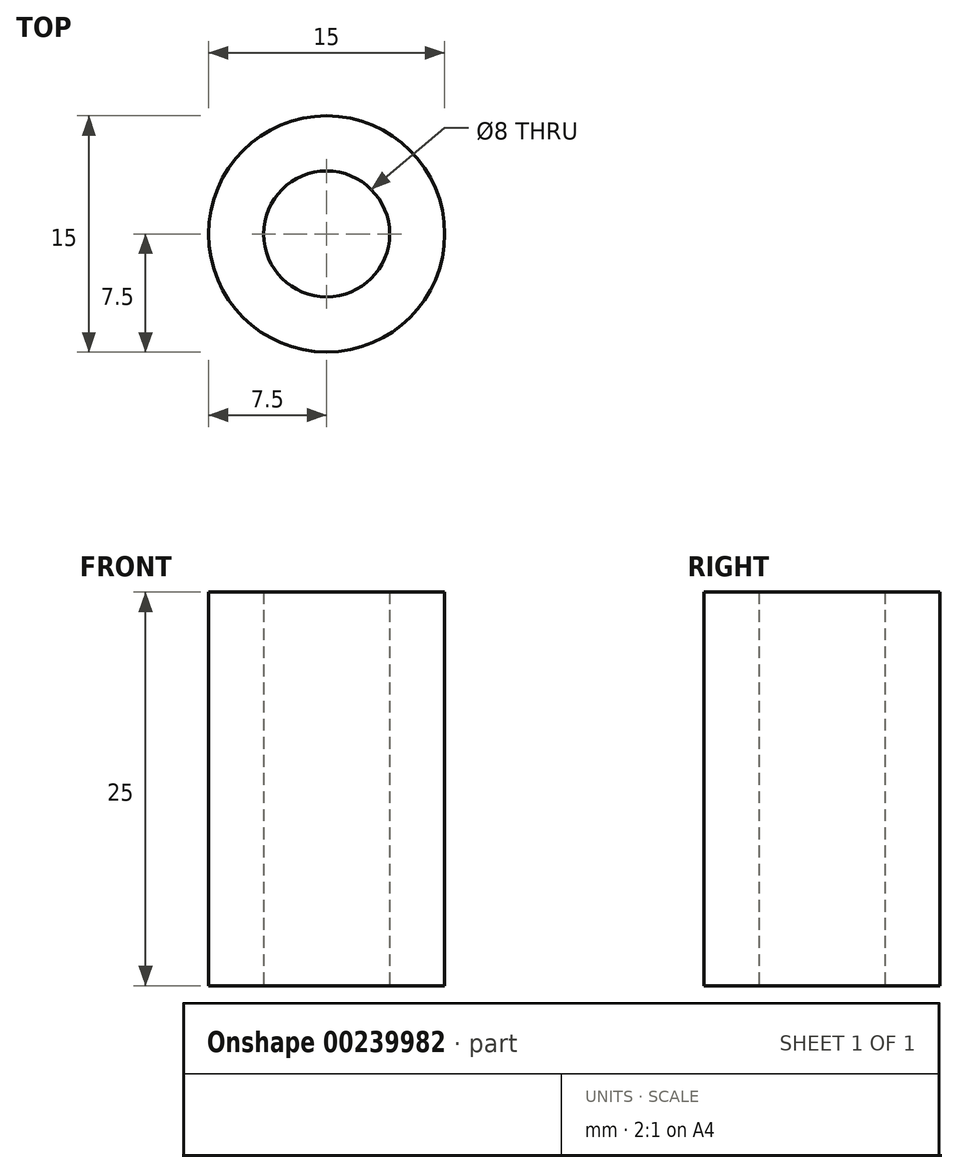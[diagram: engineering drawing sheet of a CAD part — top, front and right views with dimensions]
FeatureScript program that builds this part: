
annotation { "Feature Type Name" : "Feature", "Feature Type Description" : "" }
export const myFeature = defineFeature(function(context is Context, id is Id, definition is map)
    precondition{}
    {
        {
            var Q0;
            Q0=qCreatedBy(makeId("Top.planeOp"),FACE);
            var sketch = newSketch(context, id + "F0", { "sketchPlane" : qUnion([Q0])});
            skCircle(sketch, "E0", {"center": v(0, 0) * mm, "radius": 4 * mm});
            skCircle(sketch, "E1", {"center": v(0, 0) * mm, "radius": 7.5 * mm});
            skSolve(sketch);
        }
        {
            var Q0;
            Q0=makeQuery(id+"F0.imprint","IMPRINT",FACE,{"disambiguationData":[TD([[makeQuery(id+"F0.imprint","IMPRINT",EDGE,{"derivedFrom":sQuery(id+"F0.wireOp",EDGE,"E0")}),-1.0]])]});
            extrude(context, id + "F1", {"entities" : qUnion([Q0]), "depth" : 25 * mm});
        }
    });
